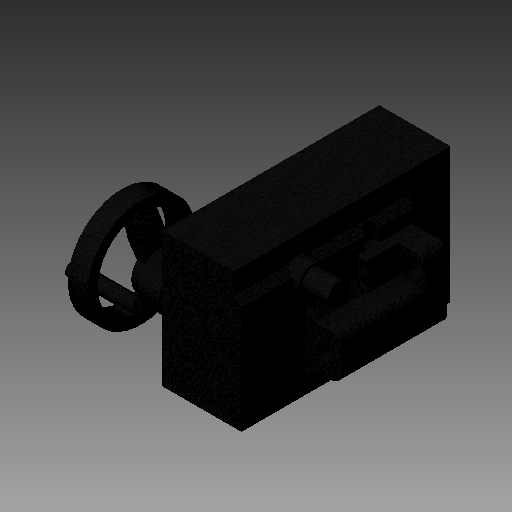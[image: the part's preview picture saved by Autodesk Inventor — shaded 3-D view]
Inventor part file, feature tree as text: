
AUTODESK INVENTOR PART (.ipt)
format: ipt  version: 2018 (Build 220112000, 112)  size: 594,944 bytes
history: native  units: in
note: dims shown in document units (in); Inventor stores cm internally (conversion verified against a paired STEP export)
features: sketch x19, extrude x16, fillet x6, plane x3, loft x2, chamfer x1, other x1, projected_geometry x1
ambient origin geometry x8: Origin, YZ Plane, XZ Plane, XY Plane, X Axis, Y Axis, Z Axis, Center Point
bodies: Solid1 (feature_tree)
feature tree (49):
  extrude  "Extrusion1"  Depth=4.3701in
  extrude  "Extrusion2"  Depth=1.1811in
  extrude  "Extrusion3"  Depth=12.0079in TaperAngle=0.0deg
  extrude  "Extrusion4"  Depth=12.0079in TaperAngle=0.0deg
  extrude  "Extrusion5"  Depth=1.9685in
  extrude  "Extrusion6"  Depth=1.4567in TaperAngle=0.0deg
  extrude  "Extrusion7"  Depth=4.6457in TaperAngle=0.0deg
  fillet  "Fillet2"  Radius=1.7717in
  chamfer  "Chamfer1"  Distance=0.5512in
  fillet  "Fillet3"  Radius=0.7874in
  extrude  "Extrusion8"  Depth=0.5118in TaperAngle=0.0deg
  extrude  "Extrusion9"  Depth=0.315in
  extrude  "Extrusion10"  Depth=0.2559in TaperAngle=0.0deg
  fillet  "Fillet4"  Radius=0.5906in
  extrude  "Extrusion11"  Depth=0.0787in
  extrude  "Extrusion12"  Depth=0.0787in
  plane  "Work Plane2"
  loft  "Loft1"
  plane  "Work Plane3"
  extrude  "Extrusion13"  Depth=1.1417in
  extrude  "Extrusion15"  Depth=1.7717in
  plane  "Work Plane5"
  sketch  "Sketch22"  dims[d50=1.2205in d51=1.4173in d52=0.0in d53=0.1181in d54=2.7559in]
  sketch  "Sketch16"  dims[d41=0.9646in d42=1.1417in]
  loft  "Loft2"
  fillet  "Fillet5"  Radius=0.8268in
  extrude  "Extrusion16"  Depth=1.4173in TaperAngle=0.0deg
  fillet  "Fillet6"  Radius=0.1181in
  fillet  "Fillet7"  Radius=2.7559in
  extrude  "Extrusion17"  Depth=1.1811in
  sketch  "Sketch1"  dims[d0=3.937in d1=4.3701in]
  sketch  "Sketch2"  dims[d2=7.4803in d3=1.1811in]
  sketch  "Sketch3"  dims[d4=5.9843in d5=12.0079in d6=0.0in]
  sketch  "Sketch4"  dims[d7=2.3228in d8=12.0079in d9=0.0in]
  sketch  "Sketch5"  dims[d10=0.7087in d11=1.9685in]
  sketch  "Sketch6"  dims[d12=3.8976in d13=1.4567in d14=0.0in]
  sketch  "Sketch7"  dims[d15=1.5748in d16=4.6457in d17=0.0in d18=1.7717in d19=0.5512in d20=0.0in d21=0.7874in]
  sketch  "Sketch9"  dims[d22=0.7874in d23=0.5118in d24=0.0in]
  sketch  "Sketch10"  dims[d25=2.3622in d26=0.315in]
  sketch  "Sketch11"  dims[d27=0.5906in d28=0.2559in d29=0.0in d31=0.5906in]
  sketch  "Sketch12"  dims[d32=0.5118in d33=0.0787in d34=45.0deg d36=1.1811in]
  sketch  "Sketch13"  dims[d37=1.6142in d38=0.0787in]
  sketch  "Sketch15"  dims[d39=0.9449in d40=0.7874in]
  other  "Edges1"
  sketch  "Sketch18"  dims[d43=0.2559in d44=0.0in d45=1.7717in]
  sketch  "Sketch21"  dims[d46=1.5748in d47=3.5827in d48=0.8268in d49=0.0in]
  projected_geometry  "Projected Loop4"
  sketch  "Sketch23"  dims[d55=3.3071in d56=1.1811in]
  sketch  "Sketch24"  dims[d57=1.1417in d58=0.0in d59=2.2047in d60=0.2756in d61=0.0in d62=0.9449in d63=5.1181in d64=0.0in d65=90.0deg d66=0.0in d67=90.0deg d68=0.6693in d69=2.2047in d71=0.0in d72=90.0deg d75=2.2047in d76=4.7244in d78=0.7874in d79=0.5118in d80=0.2756in d81=0.0in d82=2.7559in d87=5.9843in d88=4.8031in d89=1.063in d90=0.0in d91=1.7717in d92=0.0in d93=90.0deg d94=0.5906in d95=0.7874in d96=2.2047in d97=1.063in d98=0.0in d99=0.0787in d100=0.0787in d101=2.7559in d102=0.0in]
